# Revit family: Tasklight
name_source: partatom
category: Furniture
revit_build: Autodesk Revit Architecture 2012 (Build: 20110916_2132(x64)
units: mm (PartAtom-declared; Revit-internal decimal feet)

## types (1)
- Tasklight
    Assembly Code = D5030900
    Cost - Level1 = 0
    Cost - Level2 = 0
    Cost - Level3 = 0
    Current = 0
    Depth = 18"
    Description = ARTICULATING TASK LIGHT TO BE MOUNTED AT TOP REAR OF CONSOLE
    Heat Load Active = 0
    Heat Load Standby = 0
    Height = 0"
    Model = TASK LIGHT
    Noise = 0
    Power Active = 0
    Power Factor (%) = 0
    Power Peak = 0
    Power Standby = 0
    Power Voltage = 0
    Product Name = TASK LIGHT
    Safety Rating = UL
    Seismic Rating = UBC IBC CBC ASCE and NFPA Zone 4 and Use Group III OSHPD
    Sustainability Rating = RoHS GREENGUARD IAQ for Children and Schools
    Task Light = Black Metal
    URL = www.therevitcollection.com
    Weight DIM = 0
    Weight Product = 0
    Width = 15"

## geometry (parser evidence)
native form markers: Blend x2, Sweep x2
no freeform markers — native parametric forms only
